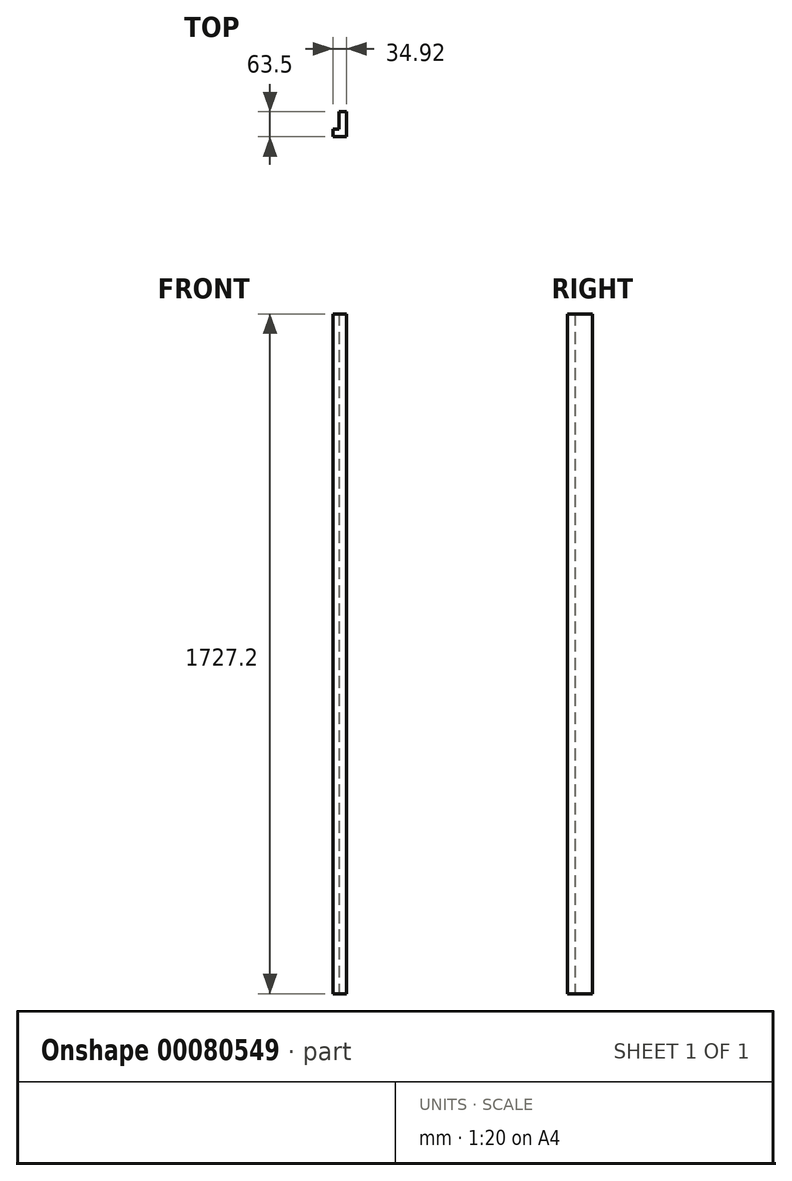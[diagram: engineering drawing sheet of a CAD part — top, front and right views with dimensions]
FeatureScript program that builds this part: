
annotation { "Feature Type Name" : "Feature", "Feature Type Description" : "" }
export const myFeature = defineFeature(function(context is Context, id is Id, definition is map)
    precondition{}
    {
        {
            var Q0;
            Q0=qCreatedBy(makeId("Top.planeOp"),FACE);
            var sketch = newSketch(context, id + "F0", { "sketchPlane" : qUnion([Q0])});
            skLineSegment(sketch, "E0", {"start": v(0, 0) * mm, "end": v(0, -63.5) * mm});
            skLineSegment(sketch, "E1", {"start": v(0, -63.5) * mm, "end": v(-34.93, -63.5) * mm});
            skLineSegment(sketch, "E2", {"start": v(-34.93, -63.5) * mm, "end": v(-34.93, -44.45) * mm});
            skLineSegment(sketch, "E3", {"start": v(-34.93, -44.45) * mm, "end": v(-19.05, -44.45) * mm});
            skLineSegment(sketch, "E4", {"start": v(-19.05, -44.45) * mm, "end": v(-19.05, 0) * mm});
            skLineSegment(sketch, "E5", {"start": v(-19.05, 0) * mm, "end": v(0, 0) * mm});
            skSolve(sketch);
        }
        {
            var Q0;
            Q0=makeQuery(id+"F0.imprint","IMPRINT",FACE,{"disambiguationData":[TD([[makeQuery(id+"F0.imprint","IMPRINT",EDGE,{"derivedFrom":sQuery(id+"F0.wireOp",EDGE,"E0")}),-1.0]])]});
            extrude(context, id + "F1", {"entities" : qUnion([Q0]), "depth" : 1727.2 * mm});
        }
    });
